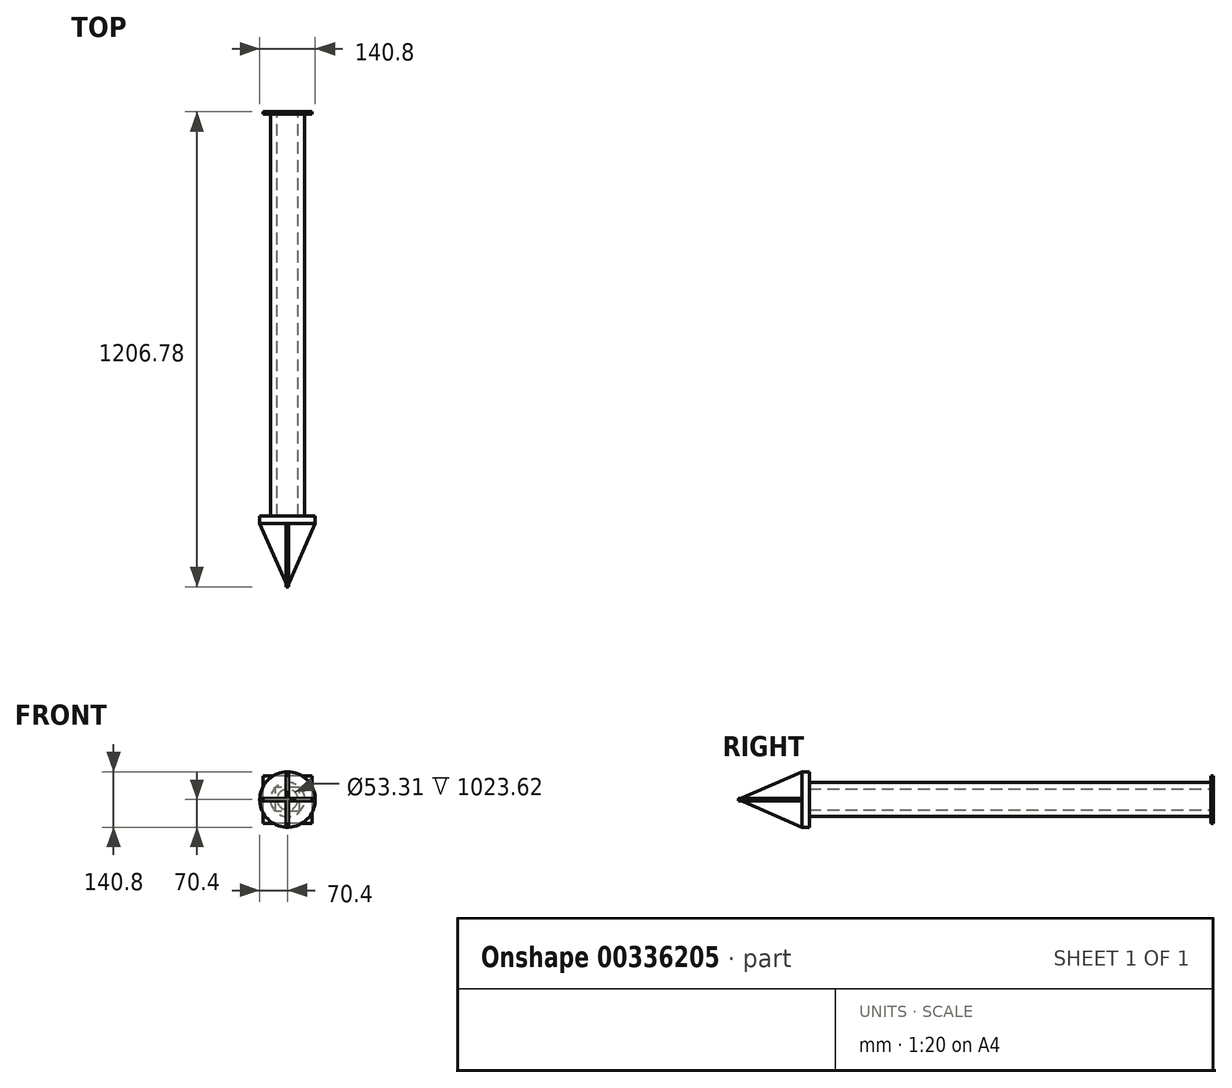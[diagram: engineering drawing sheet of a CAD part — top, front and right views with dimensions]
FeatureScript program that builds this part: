
annotation { "Feature Type Name" : "Feature", "Feature Type Description" : "" }
export const myFeature = defineFeature(function(context is Context, id is Id, definition is map)
    precondition{}
    {
        {
            var Q0;
            Q0=qCreatedBy(makeId("Front.planeOp"),FACE);
            var sketch = newSketch(context, id + "F0", { "sketchPlane" : qUnion([Q0])});
            skCircle(sketch, "E0", {"center": v(0, 0) * mm, "radius": 43.54 * mm});
            skCircle(sketch, "E1", {"center": v(0, 0) * mm, "radius": 26.66 * mm});
            skSolve(sketch);
        }
        {
            var Q0;
            Q0 = qSketchRegion(id + "F0", true);
            extrude(context, id + "F1", {"entities" : qUnion([Q0]), "depth" : 1023.62 * mm});
        }
        {
            var Q0;
            Q0=makeQuery(id+"F1.opExtrude","CAP_FACE",FACE,{"disambiguationData":[OSD([sQuery(id+"F0.wireOp",EDGE,"E0"),sQuery(id+"F0.wireOp",EDGE,"E1")])],"isStart":false});
            cPlane(context, id + "F2", {"entities" : qUnion([Q0]), "cplaneType" : CPlaneType.OFFSET, "offset" : 0 * mm, "width" : 152.4 * mm, "height" : 152.4 * mm});
        }
        {
            var Q0;
            Q0=qCreatedBy(id+"F2.planeOp",FACE);
            var sketch = newSketch(context, id + "F3", { "sketchPlane" : qUnion([Q0])});
            skCircle(sketch, "E2", {"center": v(0, 0) * mm, "radius": 70.4 * mm});
            skSolve(sketch);
        }
        {
            var Q0;
            Q0 = qSketchRegion(id + "F3", true);
            extrude(context, id + "F4", {"entities" : qUnion([Q0]), "operationType" : NewBodyOperationType.ADD, "depth" : 19.05 * mm});
        }
        {
            var Q0;
            Q0=qCreatedBy(makeId("Right.planeOp"),FACE);
            var sketch = newSketch(context, id + "F5", { "sketchPlane" : qUnion([Q0])});
            skLineSegment(sketch, "E3", {"start": v(-1042.67, 0) * mm, "end": v(-1203.6, 0) * mm});
            skLineSegment(sketch, "E4", {"start": v(-1203.6, 0) * mm, "end": v(-1042.67, 70.18) * mm});
            skLineSegment(sketch, "E5", {"start": v(-1042.67, 70.18) * mm, "end": v(-1042.67, -70.4) * mm});
            skLineSegment(sketch, "E6", {"start": v(-1042.67, -70.4) * mm, "end": v(-1203.6, 0) * mm});
            skSolve(sketch);
        }
        {
            var Q0;
            Q0=qCreatedBy(makeId("Top.planeOp"),FACE);
            var sketch = newSketch(context, id + "F6", { "sketchPlane" : qUnion([Q0])});
            skLineSegment(sketch, "E7", {"start": v(-70.4, -1042.67) * mm, "end": v(70.4, -1042.67) * mm});
            skLineSegment(sketch, "E8", {"start": v(70.4, -1042.67) * mm, "end": v(0, -1203.45) * mm});
            skLineSegment(sketch, "E9", {"start": v(0, -1203.45) * mm, "end": v(-70.4, -1042.67) * mm});
            skSolve(sketch);
        }
        {
            var Q0;
            Q0=makeQuery(id+"F6.imprint","IMPRINT",FACE,{"disambiguationData":[TD([[makeQuery(id+"F6.imprint","IMPRINT",EDGE,{"derivedFrom":sQuery(id+"F6.wireOp",EDGE,"E7")}),-1.0]])]});
            extrude(context, id + "F7", {"entities" : qUnion([Q0]), "endBound" : BoundingType.SYMMETRIC, "depth" : 6.35 * mm});
        }
        {
            var Q0;
            {var subQ0=sQuery(id+"F5.wireOp",EDGE,"E3");Q0=makeQuery(id+"F5.imprint","IMPRINT",FACE,{"disambiguationData":[TD([[makeQuery(id+"F5.imprint","IMPRINT",EDGE,{"derivedFrom":subQ0}),1.0]])]});}
            var Q1;
            {var subQ0=sQuery(id+"F5.wireOp",EDGE,"E3");Q1=makeQuery(id+"F5.imprint","IMPRINT",FACE,{"disambiguationData":[TD([[makeQuery(id+"F5.imprint","IMPRINT",EDGE,{"derivedFrom":subQ0}),-1.0]])]});}
            extrude(context, id + "F8", {"entities" : qUnion([Q0, Q1]), "endBound" : BoundingType.SYMMETRIC, "depth" : 6.35 * mm});
        }
        {
            var Q0;
            Q0=qCreatedBy(makeId("Front.planeOp"),FACE);
            var sketch = newSketch(context, id + "F9", { "sketchPlane" : qUnion([Q0])});
            skLineSegment(sketch, "E10.bottom", {"start": v(-30.9, 30.22) * mm, "end": v(30.9, 30.22) * mm});
            skLineSegment(sketch, "E10.top", {"start": v(-30.9, -30.22) * mm, "end": v(30.9, -30.22) * mm});
            skLineSegment(sketch, "E10.left", {"start": v(-30.9, 30.22) * mm, "end": v(-30.9, -30.22) * mm});
            skLineSegment(sketch, "E10.right", {"start": v(30.9, 30.22) * mm, "end": v(30.9, -30.22) * mm});
            skPoint(sketch, "E10.middle", {"position": v(0, 0) * mm});
            skLineSegment(sketch, "E11.bottom", {"start": v(0, 0) * mm, "end": v(-61.8, 0) * mm});
            skLineSegment(sketch, "E11.top", {"start": v(0, 60.44) * mm, "end": v(-61.8, 60.44) * mm});
            skLineSegment(sketch, "E11.left", {"start": v(0, 0) * mm, "end": v(0, 60.44) * mm});
            skLineSegment(sketch, "E11.right", {"start": v(-61.8, 0) * mm, "end": v(-61.8, 60.44) * mm});
            skPoint(sketch, "E11.middle", {"position": v(-30.9, 30.22) * mm});
            skLineSegment(sketch, "E12.top", {"start": v(0, -60.44) * mm, "end": v(-61.8, -60.44) * mm});
            skLineSegment(sketch, "E12.left", {"start": v(0, 0) * mm, "end": v(0, -60.44) * mm});
            skLineSegment(sketch, "E12.right", {"start": v(-61.8, 0) * mm, "end": v(-61.8, -60.44) * mm});
            skPoint(sketch, "E12.middle", {"position": v(-30.9, -30.22) * mm});
            skLineSegment(sketch, "E13.bottom", {"start": v(0, 0) * mm, "end": v(61.8, 0) * mm});
            skLineSegment(sketch, "E13.top", {"start": v(0, -60.44) * mm, "end": v(61.8, -60.44) * mm});
            skLineSegment(sketch, "E13.right", {"start": v(61.8, 0) * mm, "end": v(61.8, -60.44) * mm});
            skPoint(sketch, "E13.middle", {"position": v(30.9, -30.22) * mm});
            skLineSegment(sketch, "E14.top", {"start": v(0, 60.44) * mm, "end": v(61.8, 60.44) * mm});
            skLineSegment(sketch, "E14.right", {"start": v(61.8, 0) * mm, "end": v(61.8, 60.44) * mm});
            skPoint(sketch, "E14.middle", {"position": v(30.9, 30.22) * mm});
            skSolve(sketch);
        }
        {
            var Q0;
            {var subQ0=sQuery(id+"F9.wireOp",EDGE,"E11.top");Q0=makeQuery(id+"F9.imprint","IMPRINT",FACE,{"disambiguationData":[TD([[makeQuery(id+"F9.imprint","IMPRINT",EDGE,{"derivedFrom":subQ0}),1.0]])]});}
            var Q1;
            {var subQ7=sQuery(id+"F9.wireOp",EDGE,"E12.top");Q1=makeQuery(id+"F9.imprint","IMPRINT",FACE,{"disambiguationData":[TD([[makeQuery(id+"F9.imprint","IMPRINT",EDGE,{"derivedFrom":subQ7}),-1.0]])]});}
            var Q2;
            {var subQ1=sQuery(id+"F9.wireOp",EDGE,"E13.top");Q2=makeQuery(id+"F9.imprint","IMPRINT",FACE,{"disambiguationData":[TD([[makeQuery(id+"F9.imprint","IMPRINT",EDGE,{"derivedFrom":subQ1}),1.0]])]});}
            var Q3;
            {var subQ0=sQuery(id+"F9.wireOp",EDGE,"E14.top");Q3=makeQuery(id+"F9.imprint","IMPRINT",FACE,{"disambiguationData":[TD([[makeQuery(id+"F9.imprint","IMPRINT",EDGE,{"derivedFrom":subQ0}),-1.0]])]});}
            extrude(context, id + "F10", {"entities" : qUnion([Q0, Q1, Q2, Q3]), "operationType" : NewBodyOperationType.ADD, "endBound" : BoundingType.SYMMETRIC, "depth" : 6.35 * mm});
        }
    });
